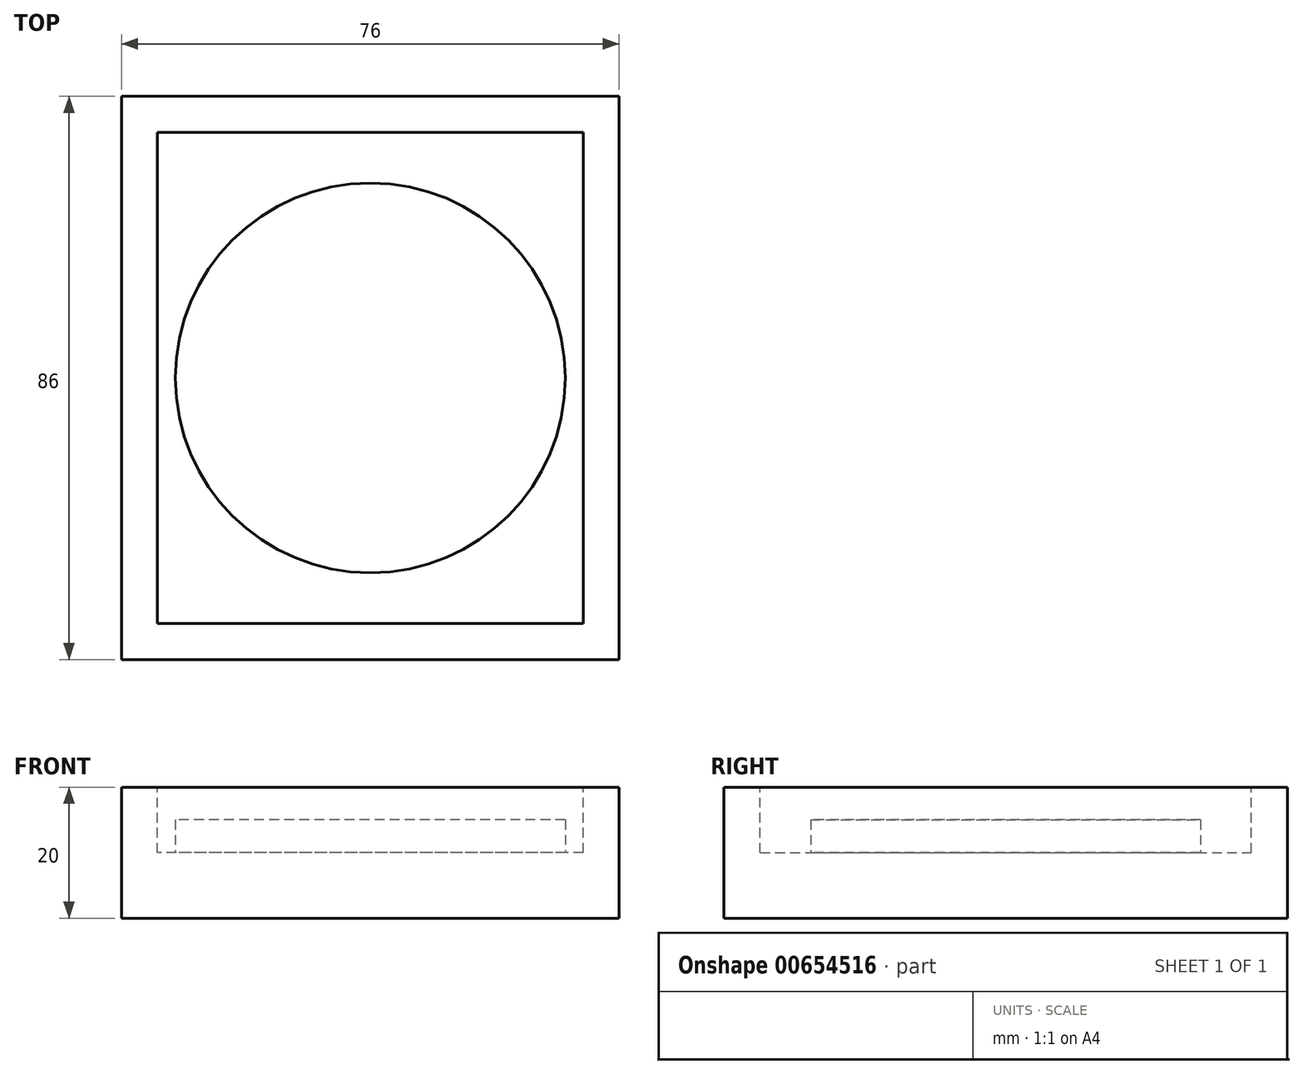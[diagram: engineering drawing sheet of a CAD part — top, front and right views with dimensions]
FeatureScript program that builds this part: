
annotation { "Feature Type Name" : "Feature", "Feature Type Description" : "" }
export const myFeature = defineFeature(function(context is Context, id is Id, definition is map)
    precondition{}
    {
        {
            var Q0;
            Q0=qCreatedBy(makeId("Top.planeOp"),FACE);
            var sketch = newSketch(context, id + "F0", { "sketchPlane" : qUnion([Q0])});
            skLineSegment(sketch, "E0.bottom", {"start": v(-38, 43) * mm, "end": v(38, 43) * mm});
            skLineSegment(sketch, "E0.top", {"start": v(-38, -43) * mm, "end": v(38, -43) * mm});
            skLineSegment(sketch, "E0.left", {"start": v(-38, 43) * mm, "end": v(-38, -43) * mm});
            skLineSegment(sketch, "E0.right", {"start": v(38, 43) * mm, "end": v(38, -43) * mm});
            skPoint(sketch, "E0.middle", {"position": v(0, 0) * mm});
            skSolve(sketch);
        }
        {
            var Q0;
            Q0 = qSketchRegion(id + "F0", true);
            extrude(context, id + "F1", {"entities" : qUnion([Q0]), "depth" : 20 * mm, "offsetDistance" : 25.4 * mm});
        }
        {
            var Q0;
            Q0=makeQuery(id+"F1.opExtrude","CAP_FACE",FACE,{"disambiguationData":[OSD([sQuery(id+"F0.wireOp",EDGE,"E0.bottom"),sQuery(id+"F0.wireOp",EDGE,"E0.top"),sQuery(id+"F0.wireOp",EDGE,"E0.left"),sQuery(id+"F0.wireOp",EDGE,"E0.right")])],"isStart":false});
            var sketch = newSketch(context, id + "F2", { "sketchPlane" : qUnion([Q0])});
            skLineSegment(sketch, "E1.bottom", {"start": v(32.5, -37.5) * mm, "end": v(-32.5, -37.5) * mm});
            skLineSegment(sketch, "E1.top", {"start": v(32.5, 37.5) * mm, "end": v(-32.5, 37.5) * mm});
            skLineSegment(sketch, "E1.left", {"start": v(32.5, -37.5) * mm, "end": v(32.5, 37.5) * mm});
            skLineSegment(sketch, "E1.right", {"start": v(-32.5, -37.5) * mm, "end": v(-32.5, 37.5) * mm});
            skPoint(sketch, "E1.middle", {"position": v(0, 0) * mm});
            skSolve(sketch);
        }
        {
            var Q0;
            Q0 = qSketchRegion(id + "F2", true);
            extrude(context, id + "F3", {"entities" : qUnion([Q0]), "operationType" : NewBodyOperationType.REMOVE, "oppositeDirection" : true, "depth" : 10 * mm, "offsetDistance" : 25.4 * mm});
        }
        {
            var Q0;
            Q0=makeQuery(id+"F3.boolean.opBoolean","COPY",FACE,{"derivedFrom":makeQuery(id+"F3.opExtrude","CAP_FACE",FACE,{"disambiguationData":[OSD([sQuery(id+"F2.wireOp",EDGE,"E1.bottom"),sQuery(id+"F2.wireOp",EDGE,"E1.top"),sQuery(id+"F2.wireOp",EDGE,"E1.left"),sQuery(id+"F2.wireOp",EDGE,"E1.right")])],"isStart":false})});
            var sketch = newSketch(context, id + "F4", { "sketchPlane" : qUnion([Q0])});
            skCircle(sketch, "E2", {"center": v(0, 0) * mm, "radius": 29.77 * mm});
            skSolve(sketch);
        }
        {
            var Q0;
            Q0 = qSketchRegion(id + "F4", true);
            extrude(context, id + "F5", {"entities" : qUnion([Q0]), "operationType" : NewBodyOperationType.ADD, "depth" : 5 * mm, "offsetDistance" : 25.4 * mm});
        }
    });
